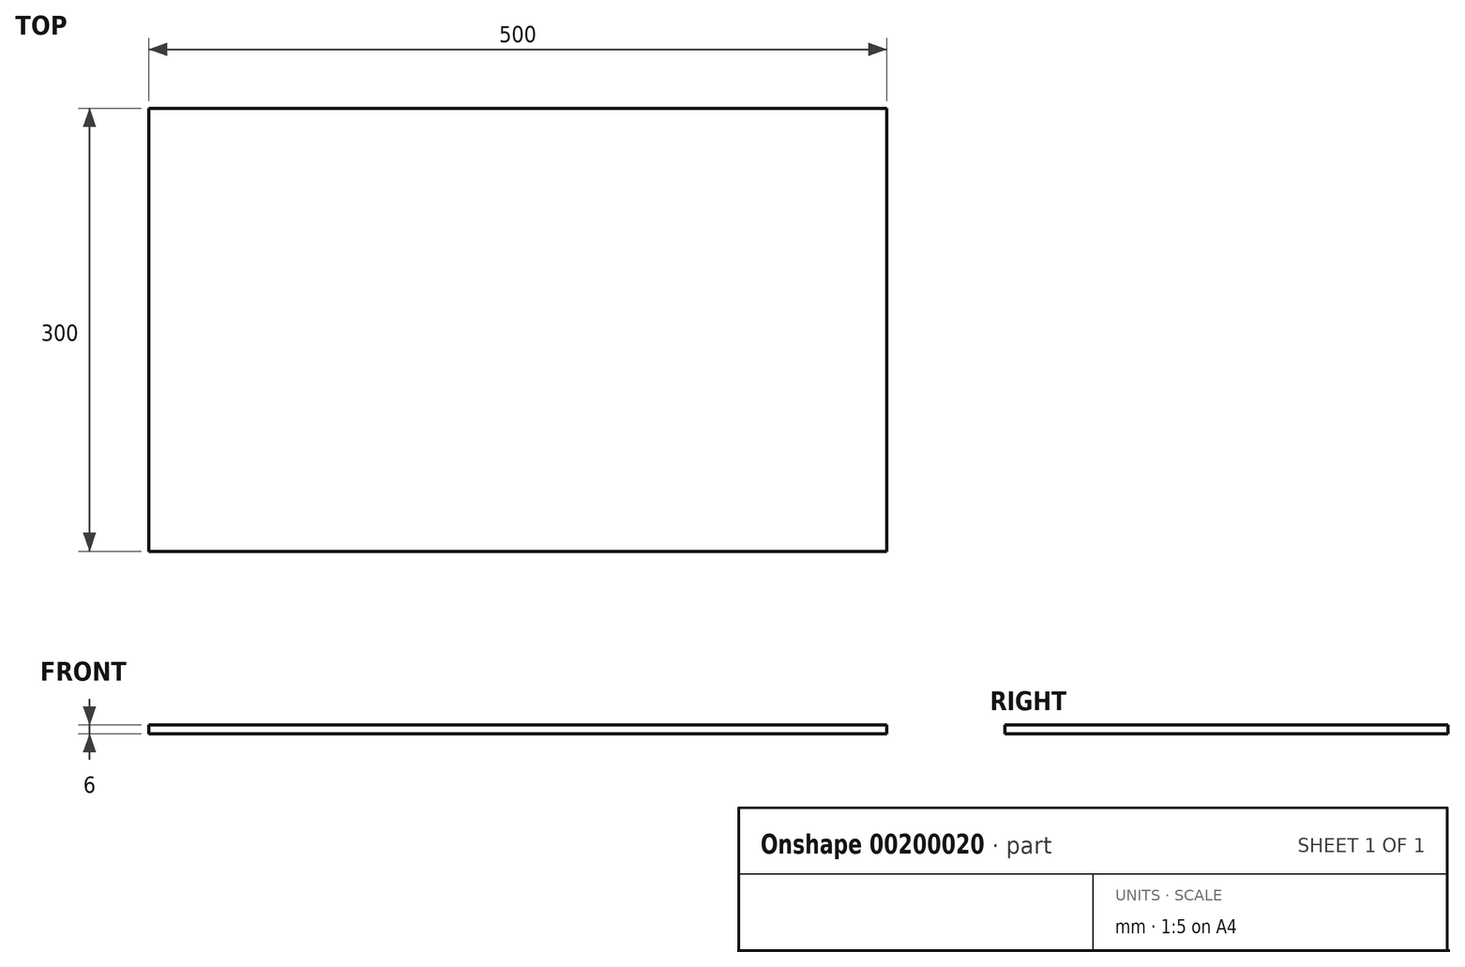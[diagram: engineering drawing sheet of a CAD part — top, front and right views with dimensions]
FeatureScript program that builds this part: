
annotation { "Feature Type Name" : "Feature", "Feature Type Description" : "" }
export const myFeature = defineFeature(function(context is Context, id is Id, definition is map)
    precondition{}
    {
        {
            var Q0;
            Q0=qCreatedBy(makeId("Top.planeOp"),FACE);
            var sketch = newSketch(context, id + "F0", { "sketchPlane" : qUnion([Q0])});
            skLineSegment(sketch, "E0.bottom", {"start": v(-250, 150) * mm, "end": v(250, 150) * mm});
            skLineSegment(sketch, "E0.top", {"start": v(-250, -150) * mm, "end": v(250, -150) * mm});
            skLineSegment(sketch, "E0.left", {"start": v(-250, 150) * mm, "end": v(-250, -150) * mm});
            skLineSegment(sketch, "E0.right", {"start": v(250, 150) * mm, "end": v(250, -150) * mm});
            skSolve(sketch);
        }
        {
            var Q0;
            Q0=makeQuery(id+"F0.imprint","IMPRINT",FACE,{"disambiguationData":[TD([[makeQuery(id+"F0.imprint","IMPRINT",EDGE,{"derivedFrom":sQuery(id+"F0.wireOp",EDGE,"E0.bottom")}),-1.0]])]});
            extrude(context, id + "F1", {"entities" : qUnion([Q0]), "depth" : 6 * mm});
        }
    });
